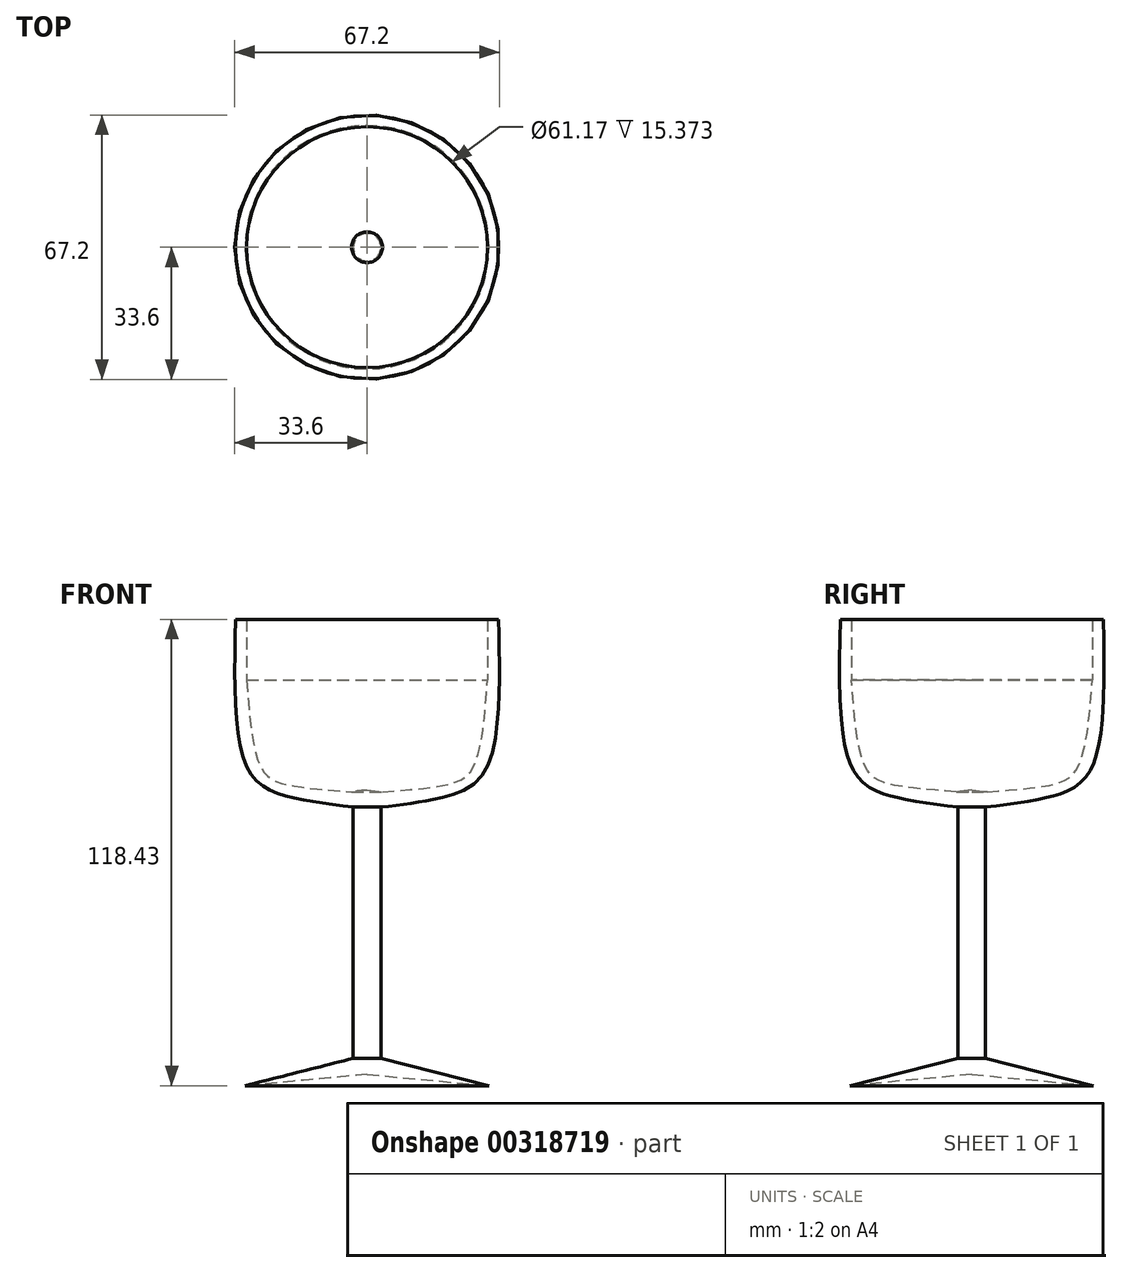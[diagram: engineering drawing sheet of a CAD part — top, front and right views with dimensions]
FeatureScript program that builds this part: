
annotation { "Feature Type Name" : "Feature", "Feature Type Description" : "" }
export const myFeature = defineFeature(function(context is Context, id is Id, definition is map)
    precondition{}
    {
        {
            var Q0;
            Q0=qCreatedBy(makeId("Front.planeOp"),FACE);
            var sketch = newSketch(context, id + "F0", { "sketchPlane" : qUnion([Q0])});
            skLineSegment(sketch, "E0", {"start": v(0, -75.93) * mm, "end": v(0, 75.93) * mm, "construction": true});
            skLineSegment(sketch, "E1", {"start": v(0, -62.41) * mm, "end": v(-30.94, -65.26) * mm});
            skLineSegment(sketch, "E2", {"start": v(-30.94, -65.26) * mm, "end": v(0, -57.43) * mm});
            skLineSegment(sketch, "E3", {"start": v(-3.51, -58.32) * mm, "end": v(-3.51, 5.51) * mm});
            skFitSpline(sketch, "E4", {"points": [v(-3.51, 5.51) * mm, v(-20.63, 8.36) * mm, v(-30.23, 15.11) * mm, v(-33.43, 53.17) * mm], "startDerivative": vector(-60.13, 7.27) * mm, "endDerivative": vector(2.05, 102.78) * mm});
            skLineSegment(sketch, "E5", {"start": v(-33.43, 53.17) * mm, "end": v(-30.58, 53.17) * mm});
            skLineSegment(sketch, "E6", {"start": v(-30.58, 53.17) * mm, "end": v(-30.58, 37.8) * mm});
            skFitSpline(sketch, "E7", {"points": [v(-30.58, 37.8) * mm, v(-26.67, 15.11) * mm, v(-20.27, 11.2) * mm, v(-3.91, 9.42) * mm], "startDerivative": vector(4.93, -66.68) * mm, "endDerivative": vector(51.85, -3.68) * mm});
            skLineSegment(sketch, "E8", {"start": v(-3.91, 9.42) * mm, "end": v(-3.51, 5.51) * mm});
            skLineSegment(sketch, "E9", {"start": v(-3.91, 9.42) * mm, "end": v(0, 9.82) * mm});
            skLineSegment(sketch, "E10", {"start": v(0, 9.82) * mm, "end": v(0, -62.41) * mm});
            skSolve(sketch);
        }
        {
            var Q0;
            {var subQ1=sQuery(id+"F0.wireOp",EDGE,"E3");Q0=makeQuery(id+"F0.imprint","IMPRINT",FACE,{"disambiguationData":[TD([[makeQuery(id+"F0.imprint","IMPRINT",EDGE,{"derivedFrom":subQ1}),-1.0]])]});}
            var Q1;
            Q1=sQuery(id+"F0.wireOp",EDGE,"E0");
            revolve(context, id + "F1", {"entities" : qUnion([Q0]), "axis" : qUnion([Q1]), "revolveType" : RevolveType.FULL});
        }
        {
            var Q0;
            Q0=makeQuery(id+"F0.imprint","IMPRINT",FACE,{"disambiguationData":[TD([[makeQuery(id+"F0.imprint","IMPRINT",EDGE,{"derivedFrom":sQuery(id+"F0.wireOp",EDGE,"E4")}),-1.0]])]});
            var Q1;
            Q1=sQuery(id+"F0.wireOp",EDGE,"E0");
            revolve(context, id + "F2", {"operationType" : NewBodyOperationType.ADD, "entities" : qUnion([Q0]), "axis" : qUnion([Q1]), "revolveType" : RevolveType.FULL});
        }
        {
            var Q0;
            {var subQ0=sQuery(id+"F0.wireOp",EDGE,"E1");Q0=makeQuery(id+"F0.imprint","IMPRINT",FACE,{"disambiguationData":[TD([[makeQuery(id+"F0.imprint","IMPRINT",EDGE,{"derivedFrom":subQ0}),-1.0]])]});}
            var Q1;
            Q1=sQuery(id+"F0.wireOp",EDGE,"E0");
            revolve(context, id + "F3", {"operationType" : NewBodyOperationType.ADD, "entities" : qUnion([Q0]), "axis" : qUnion([Q1]), "revolveType" : RevolveType.FULL});
        }
    });
